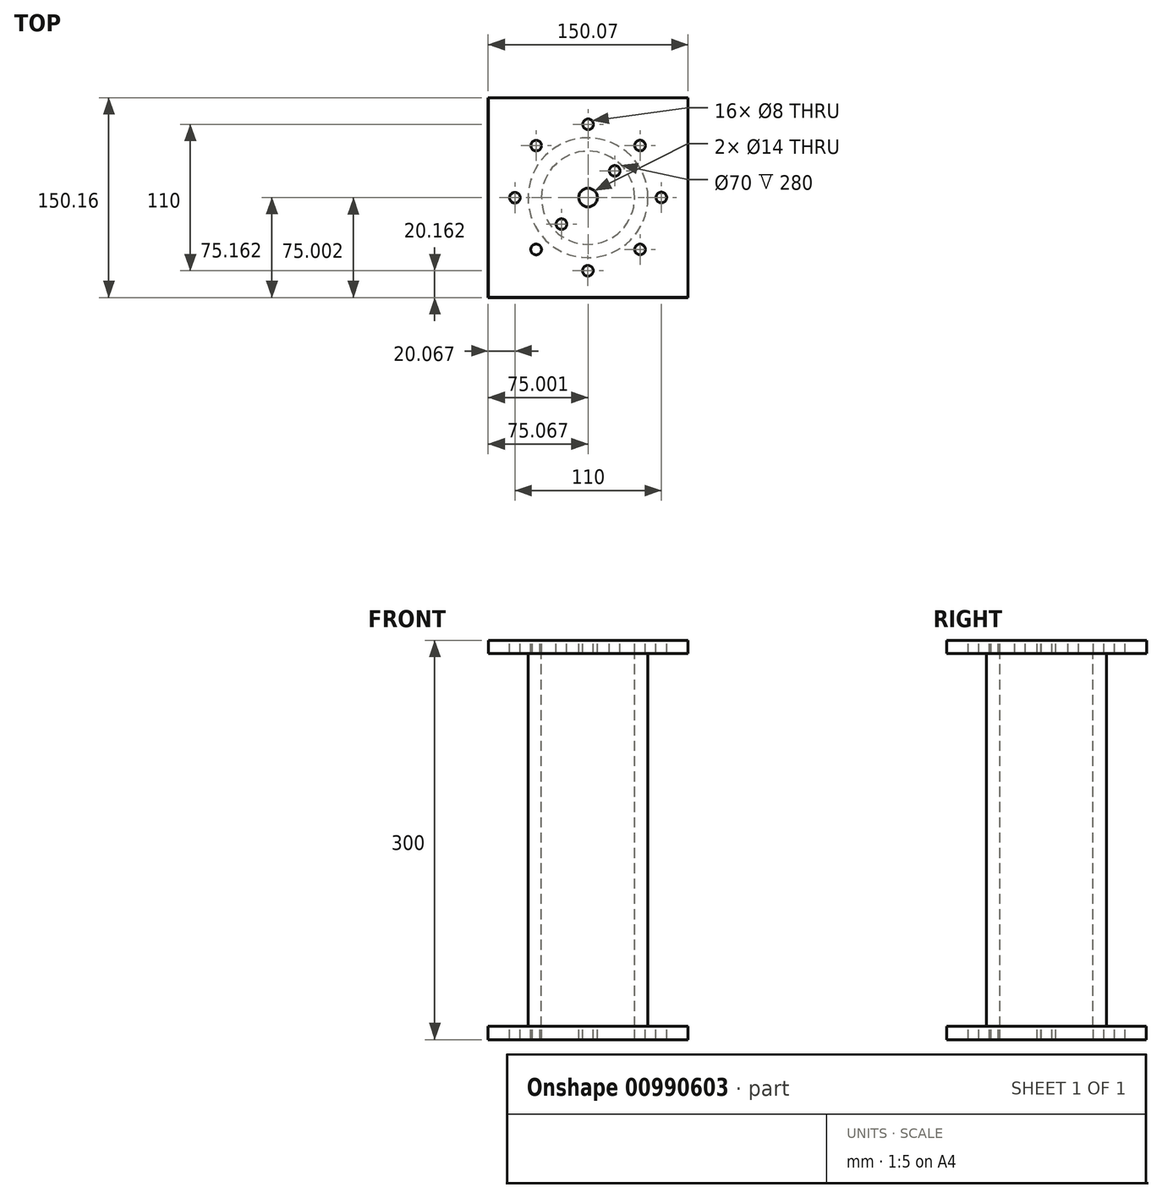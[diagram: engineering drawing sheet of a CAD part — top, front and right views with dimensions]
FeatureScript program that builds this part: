
annotation { "Feature Type Name" : "Feature", "Feature Type Description" : "" }
export const myFeature = defineFeature(function(context is Context, id is Id, definition is map)
    precondition{}
    {
        {
            var Q0;
            Q0=qCreatedBy(makeId("Top.planeOp"),FACE);
            var sketch = newSketch(context, id + "F0", { "sketchPlane" : qUnion([Q0])});
            skLineSegment(sketch, "E0.bottom", {"start": v(-77.55, 65.01) * mm, "end": v(72.45, 65.01) * mm});
            skLineSegment(sketch, "E0.top", {"start": v(-77.55, -84.99) * mm, "end": v(72.45, -84.99) * mm});
            skLineSegment(sketch, "E0.left", {"start": v(-77.55, 65.01) * mm, "end": v(-77.55, -84.99) * mm});
            skLineSegment(sketch, "E0.right", {"start": v(72.45, 65.01) * mm, "end": v(72.45, -84.99) * mm});
            skSolve(sketch);
        }
        {
            var Q0;
            Q0 = qSketchRegion(id + "F0", true);
            extrude(context, id + "F1", {"entities" : qUnion([Q0]), "depth" : 10 * mm, "offsetDistance" : 25 * mm});
        }
        {
            var Q0;
            Q0=makeQuery(id+"F1.opExtrude","CAP_FACE",FACE,{"disambiguationData":[OSD([sQuery(id+"F0.wireOp",EDGE,"E0.bottom"),sQuery(id+"F0.wireOp",EDGE,"E0.top"),sQuery(id+"F0.wireOp",EDGE,"E0.left"),sQuery(id+"F0.wireOp",EDGE,"E0.right")])],"isStart":false});
            var sketch = newSketch(context, id + "F2", { "sketchPlane" : qUnion([Q0])});
            skCircle(sketch, "E1", {"center": v(-2.55, -9.99) * mm, "radius": 45 * mm});
            skPoint(sketch, "E1.centerSnap0", {"position": v(-2.55, 65.01) * mm});
            skPoint(sketch, "E1.centerSnap1", {"position": v(72.45, -9.99) * mm});
            skSolve(sketch);
        }
        {
            var Q0;
            Q0 = qSketchRegion(id + "F2", true);
            extrude(context, id + "F3", {"entities" : qUnion([Q0]), "operationType" : NewBodyOperationType.ADD, "depth" : 280 * mm, "offsetDistance" : 25 * mm});
        }
        {
            var Q0;
            Q0=makeQuery(id+"F3.opExtrude","CAP_FACE",FACE,{"disambiguationData":[OSD([sQuery(id+"F2.wireOp",EDGE,"E1")])],"isStart":false});
            var sketch = newSketch(context, id + "F4", { "sketchPlane" : qUnion([Q0])});
            skCircle(sketch, "E2", {"center": v(-2.55, -9.99) * mm, "radius": 35 * mm});
            skSolve(sketch);
        }
        {
            var Q0;
            Q0 = qSketchRegion(id + "F4", true);
            extrude(context, id + "F5", {"entities" : qUnion([Q0]), "operationType" : NewBodyOperationType.REMOVE, "oppositeDirection" : true, "depth" : 280 * mm, "offsetDistance" : 25 * mm});
        }
        {
            var Q0;
            Q0=makeQuery(id+"F3.opExtrude","CAP_FACE",FACE,{"disambiguationData":[OSD([sQuery(id+"F2.wireOp",EDGE,"E1")])],"isStart":false});
            var sketch = newSketch(context, id + "F6", { "sketchPlane" : qUnion([Q0])});
            skLineSegment(sketch, "E3.bottom", {"start": v(-77.48, 65.17) * mm, "end": v(72.52, 65.17) * mm});
            skLineSegment(sketch, "E3.top", {"start": v(-77.48, -84.83) * mm, "end": v(72.52, -84.83) * mm});
            skLineSegment(sketch, "E3.left", {"start": v(-77.48, 65.17) * mm, "end": v(-77.48, -84.83) * mm});
            skLineSegment(sketch, "E3.right", {"start": v(72.52, 65.17) * mm, "end": v(72.52, -84.83) * mm});
            skSolve(sketch);
        }
        {
            var Q0;
            Q0 = qSketchRegion(id + "F6", true);
            extrude(context, id + "F7", {"entities" : qUnion([Q0]), "operationType" : NewBodyOperationType.ADD, "depth" : 10 * mm, "offsetDistance" : 25 * mm});
        }
        {
            var Q0;
            Q0=makeQuery(id+"F7.opExtrude","CAP_FACE",FACE,{"disambiguationData":[OSD([sQuery(id+"F6.wireOp",EDGE,"E3.bottom"),sQuery(id+"F6.wireOp",EDGE,"E3.top"),sQuery(id+"F6.wireOp",EDGE,"E3.left"),sQuery(id+"F6.wireOp",EDGE,"E3.right")])],"isStart":false});
            var sketch = newSketch(context, id + "F8", { "sketchPlane" : qUnion([Q0])});
            skCircle(sketch, "E4", {"center": v(-2.48, -9.83) * mm, "radius": 7 * mm});
            skPoint(sketch, "E4.centerSnap0", {"position": v(72.52, -9.83) * mm});
            skPoint(sketch, "E4.centerSnap1", {"position": v(-2.48, 65.17) * mm});
            skSolve(sketch);
        }
        {
            var Q0;
            Q0 = qSketchRegion(id + "F8", true);
            extrude(context, id + "F9", {"entities" : qUnion([Q0]), "operationType" : NewBodyOperationType.REMOVE, "endBound" : BoundingType.THROUGH_ALL, "oppositeDirection" : true, "depth" : 25 * mm, "offsetDistance" : 25 * mm});
        }
        {
            var Q0;
            Q0=makeQuery(id+"F7.opExtrude","CAP_FACE",FACE,{"disambiguationData":[OSD([sQuery(id+"F6.wireOp",EDGE,"E3.bottom"),sQuery(id+"F6.wireOp",EDGE,"E3.top"),sQuery(id+"F6.wireOp",EDGE,"E3.left"),sQuery(id+"F6.wireOp",EDGE,"E3.right")])],"isStart":false});
            var sketch = newSketch(context, id + "F10", { "sketchPlane" : qUnion([Q0])});
            skCircle(sketch, "E5", {"center": v(-22.48, -29.83) * mm, "radius": 4 * mm});
            skCircle(sketch, "E6", {"center": v(17.52, 10.17) * mm, "radius": 4 * mm});
            skSolve(sketch);
        }
        {
            var Q0;
            Q0 = qSketchRegion(id + "F10", true);
            extrude(context, id + "F11", {"entities" : qUnion([Q0]), "operationType" : NewBodyOperationType.REMOVE, "oppositeDirection" : true, "depth" : 25 * mm, "offsetDistance" : 25 * mm});
        }
        {
            var Q0;
            Q0=makeQuery(id+"F7.opExtrude","CAP_FACE",FACE,{"disambiguationData":[OSD([sQuery(id+"F6.wireOp",EDGE,"E3.bottom"),sQuery(id+"F6.wireOp",EDGE,"E3.top"),sQuery(id+"F6.wireOp",EDGE,"E3.left"),sQuery(id+"F6.wireOp",EDGE,"E3.right")])],"isStart":false});
            var sketch = newSketch(context, id + "F12", { "sketchPlane" : qUnion([Q0])});
            skCircle(sketch, "E7", {"center": v(-2.48, 45.17) * mm, "radius": 4 * mm});
            skCircle(sketch, "E8", {"center": v(-41.47, 29.16) * mm, "radius": 4 * mm});
            skCircle(sketch, "E9", {"center": v(-57.48, -9.99) * mm, "radius": 4 * mm});
            skCircle(sketch, "E10", {"center": v(-41.54, -48.82) * mm, "radius": 4 * mm});
            skCircle(sketch, "E11.MirrorC", {"center": v(52.52, -9.83) * mm, "radius": 4 * mm});
            skCircle(sketch, "E12.MirrorC", {"center": v(36.5, -48.82) * mm, "radius": 4 * mm});
            skCircle(sketch, "E13.MirrorC", {"center": v(-2.64, -64.83) * mm, "radius": 4 * mm});
            skCircle(sketch, "E14.MirrorC", {"center": v(-41.47, -48.88) * mm, "radius": 4 * mm});
            skCircle(sketch, "E15.MirrorC", {"center": v(36.5, 29.23) * mm, "radius": 4 * mm});
            skSolve(sketch);
        }
        {
            var Q0;
            Q0 = qSketchRegion(id + "F12", true);
            extrude(context, id + "F13", {"entities" : qUnion([Q0]), "operationType" : NewBodyOperationType.REMOVE, "endBound" : BoundingType.THROUGH_ALL, "oppositeDirection" : true, "depth" : 25 * mm, "offsetDistance" : 25 * mm});
        }
    });
